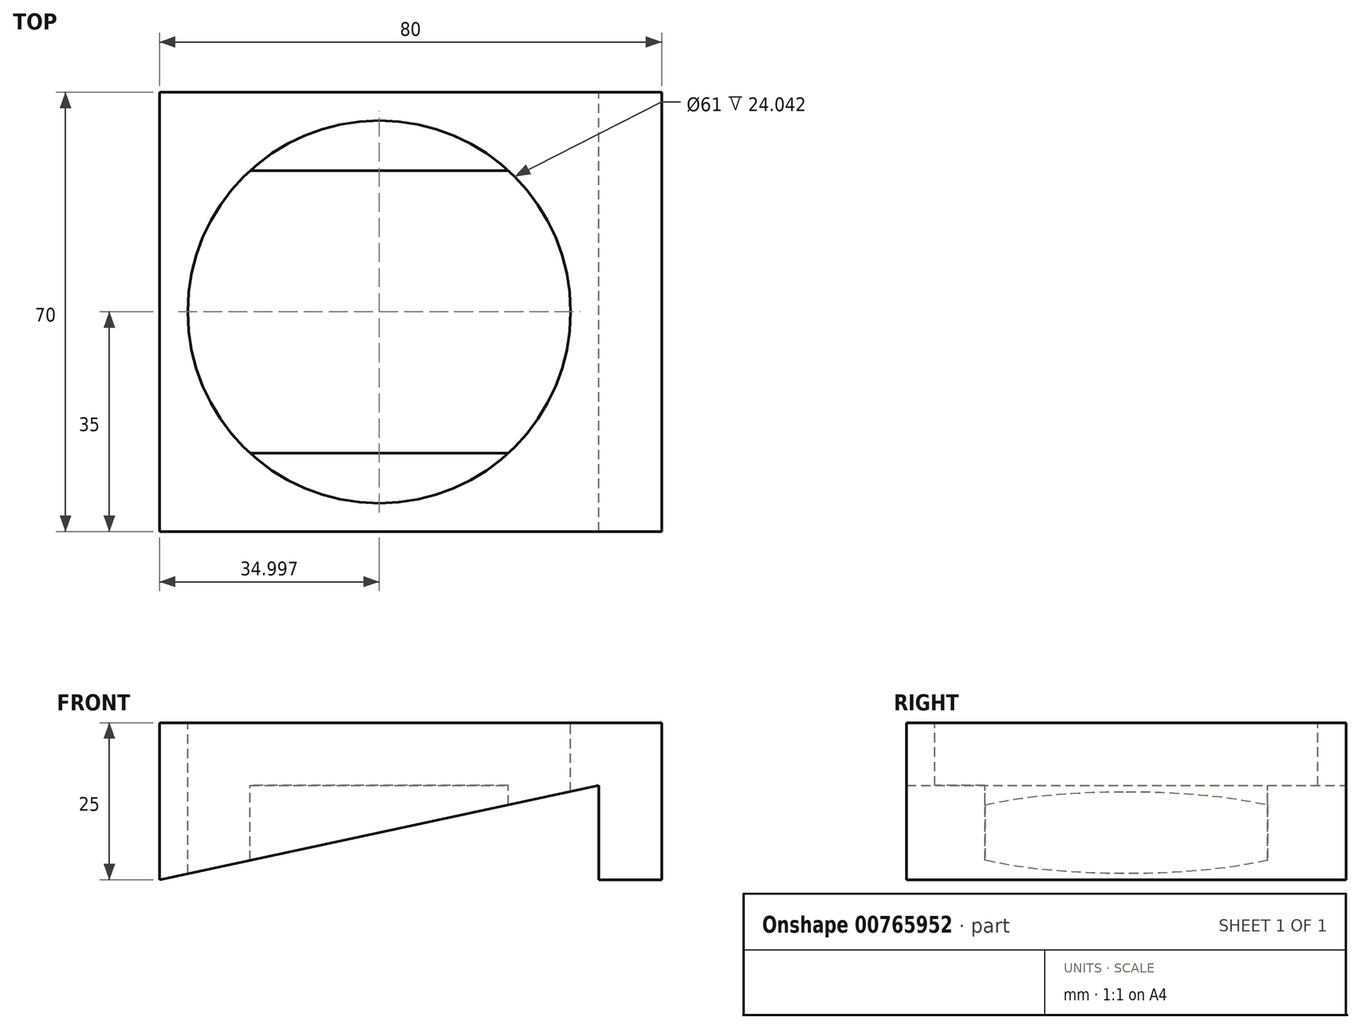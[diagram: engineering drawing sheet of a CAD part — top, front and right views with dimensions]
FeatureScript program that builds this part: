
annotation { "Feature Type Name" : "Feature", "Feature Type Description" : "" }
export const myFeature = defineFeature(function(context is Context, id is Id, definition is map)
    precondition{}
    {
        {
            var Q0;
            Q0=qCreatedBy(makeId("Front.planeOp"),FACE);
            var sketch = newSketch(context, id + "F0", { "sketchPlane" : qUnion([Q0])});
            skLineSegment(sketch, "E0", {"start": v(-78.38, 13.07) * mm, "end": v(1.62, 13.07) * mm});
            skLineSegment(sketch, "E1", {"start": v(1.62, 13.07) * mm, "end": v(1.62, -11.93) * mm});
            skLineSegment(sketch, "E2", {"start": v(1.62, -11.93) * mm, "end": v(-8.38, -11.93) * mm});
            skLineSegment(sketch, "E3", {"start": v(-8.38, -11.93) * mm, "end": v(-8.38, 3.07) * mm});
            skLineSegment(sketch, "E4", {"start": v(-78.38, 13.07) * mm, "end": v(-78.38, -11.93) * mm});
            skLineSegment(sketch, "E5", {"start": v(-78.38, -11.93) * mm, "end": v(-8.38, 3.07) * mm});
            skSolve(sketch);
        }
        {
            var Q0;
            Q0=makeQuery(id+"F0.imprint","IMPRINT",FACE,{"disambiguationData":[TD([[makeQuery(id+"F0.imprint","IMPRINT",EDGE,{"derivedFrom":sQuery(id+"F0.wireOp",EDGE,"E0")}),-1.0]])]});
            extrude(context, id + "F1", {"entities" : qUnion([Q0]), "depth" : 70 * mm, "offsetDistance" : 25 * mm});
        }
        {
            var Q0;
            Q0=makeQuery(id+"F1.opExtrude","SWEPT_FACE",FACE,{"disambiguationData":[OSD([sQuery(id+"F0.wireOp",EDGE,"E0")])]});
            var sketch = newSketch(context, id + "F2", { "sketchPlane" : qUnion([Q0])});
            skCircle(sketch, "E6", {"center": v(-43.38, -35) * mm, "radius": 30.5 * mm});
            skPoint(sketch, "E6.centerSnap0", {"position": v(-78.38, -35) * mm});
            skSolve(sketch);
        }
        {
            var Q0;
            Q0=makeQuery(id+"F2.imprint","IMPRINT",FACE,{"disambiguationData":[TD([[makeQuery(id+"F2.imprint","IMPRINT",EDGE,{"derivedFrom":sQuery(id+"F2.wireOp",EDGE,"E6")}),1.0]])]});
            extrude(context, id + "F3", {"entities" : qUnion([Q0]), "operationType" : NewBodyOperationType.REMOVE, "oppositeDirection" : true, "depth" : 10 * mm, "offsetDistance" : 25 * mm});
        }
        {
            var Q0;
            Q0=makeQuery(id+"F3.boolean.opBoolean","COPY",FACE,{"derivedFrom":makeQuery(id+"F3.opExtrude","CAP_FACE",FACE,{"disambiguationData":[OSD([sQuery(id+"F2.wireOp",EDGE,"E6")])],"isStart":false})});
            var sketch = newSketch(context, id + "F4", { "sketchPlane" : qUnion([Q0])});
            skLineSegment(sketch, "E7", {"start": v(-22.8, -12.5) * mm, "end": v(-63.97, -12.5) * mm});
            skLineSegment(sketch, "E8", {"start": v(-22.8, -57.5) * mm, "end": v(-63.97, -57.5) * mm});
            skSolve(sketch);
        }
        {
            var Q0;
            {var subQ0=sQuery(id+"F4.wireOp",EDGE,"E7");Q0=makeQuery(id+"F4.imprint","IMPRINT",FACE,{"disambiguationData":[TD([[makeQuery(id+"F4.imprint","IMPRINT",EDGE,{"derivedFrom":subQ0}),1.0]])]});}
            extrude(context, id + "F5", {"entities" : qUnion([Q0]), "operationType" : NewBodyOperationType.REMOVE, "oppositeDirection" : true, "depth" : 25 * mm, "offsetDistance" : 25 * mm});
        }
    });
